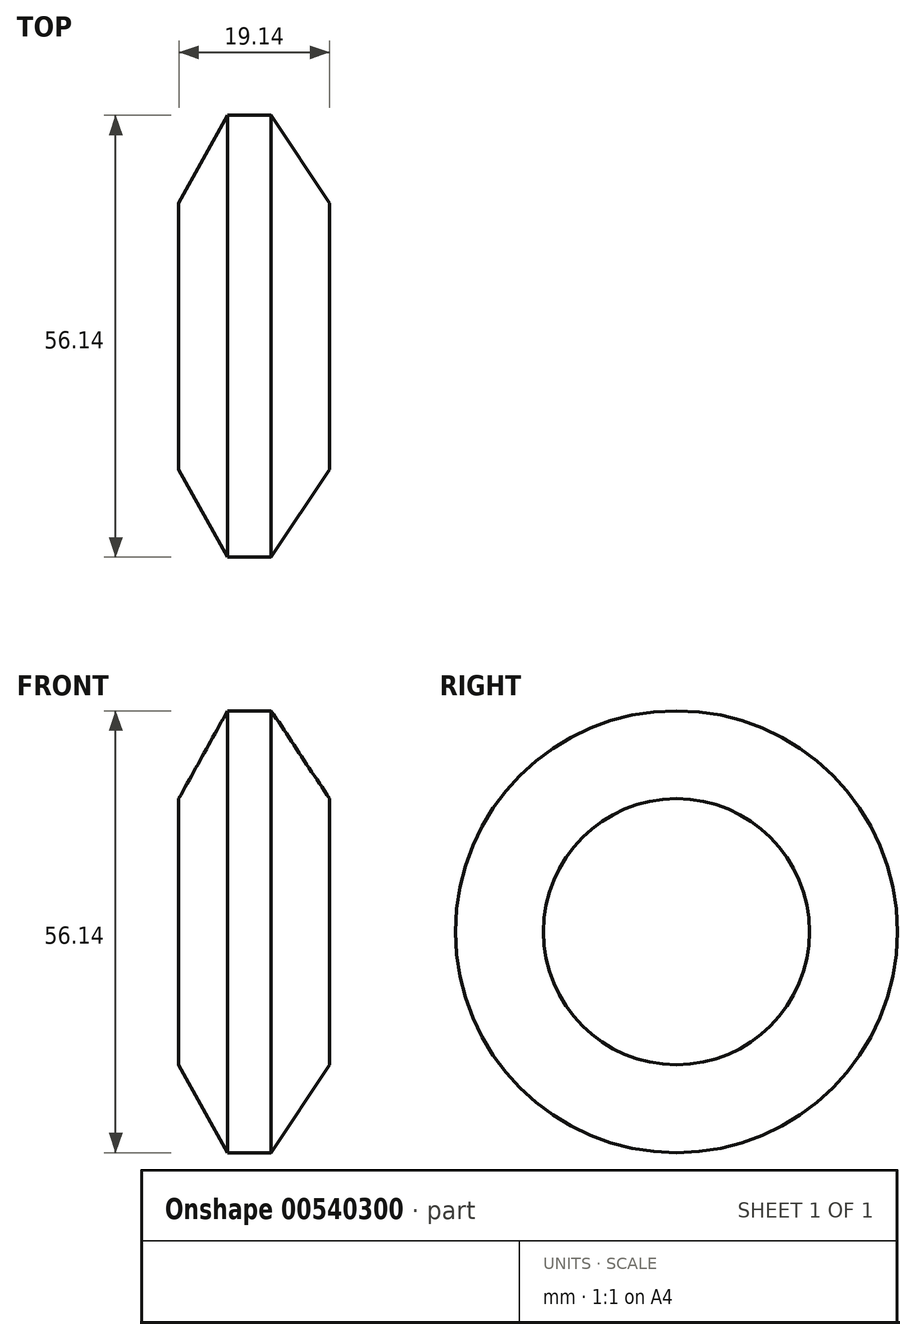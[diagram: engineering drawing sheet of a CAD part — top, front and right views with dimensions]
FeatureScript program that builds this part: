
annotation { "Feature Type Name" : "Feature", "Feature Type Description" : "" }
export const myFeature = defineFeature(function(context is Context, id is Id, definition is map)
    precondition{}
    {
        {
            var Q0;
            Q0=qCreatedBy(makeId("Front.planeOp"),FACE);
            var sketch = newSketch(context, id + "F0", { "sketchPlane" : qUnion([Q0])});
            skLineSegment(sketch, "E0", {"start": v(0, 0) * mm, "end": v(9.57, 0) * mm});
            skLineSegment(sketch, "E1", {"start": v(9.57, 0) * mm, "end": v(9.57, 16.9) * mm});
            skLineSegment(sketch, "E2", {"start": v(9.57, 16.9) * mm, "end": v(2.17, 28.07) * mm});
            skLineSegment(sketch, "E3", {"start": v(2.17, 28.07) * mm, "end": v(-3.37, 28.07) * mm});
            skLineSegment(sketch, "E4", {"start": v(-3.37, 28.07) * mm, "end": v(-9.57, 16.9) * mm});
            skLineSegment(sketch, "E5", {"start": v(-9.57, 16.9) * mm, "end": v(-9.57, 0) * mm});
            skLineSegment(sketch, "E6", {"start": v(-9.57, 0) * mm, "end": v(0, 0) * mm});
            skSolve(sketch);
        }
        {
            var Q0;
            Q0=makeQuery(id+"F0.imprint","IMPRINT",FACE,{"disambiguationData":[TD([[makeQuery(id+"F0.imprint","IMPRINT",EDGE,{"derivedFrom":sQuery(id+"F0.wireOp",EDGE,"E0")}),1.0]])]});
            var Q1;
            Q1=sQuery(id+"F0.wireOp",EDGE,"E0");
            revolve(context, id + "F1", {"entities" : qUnion([Q0]), "axis" : qUnion([Q1]), "revolveType" : RevolveType.FULL});
        }
    });
